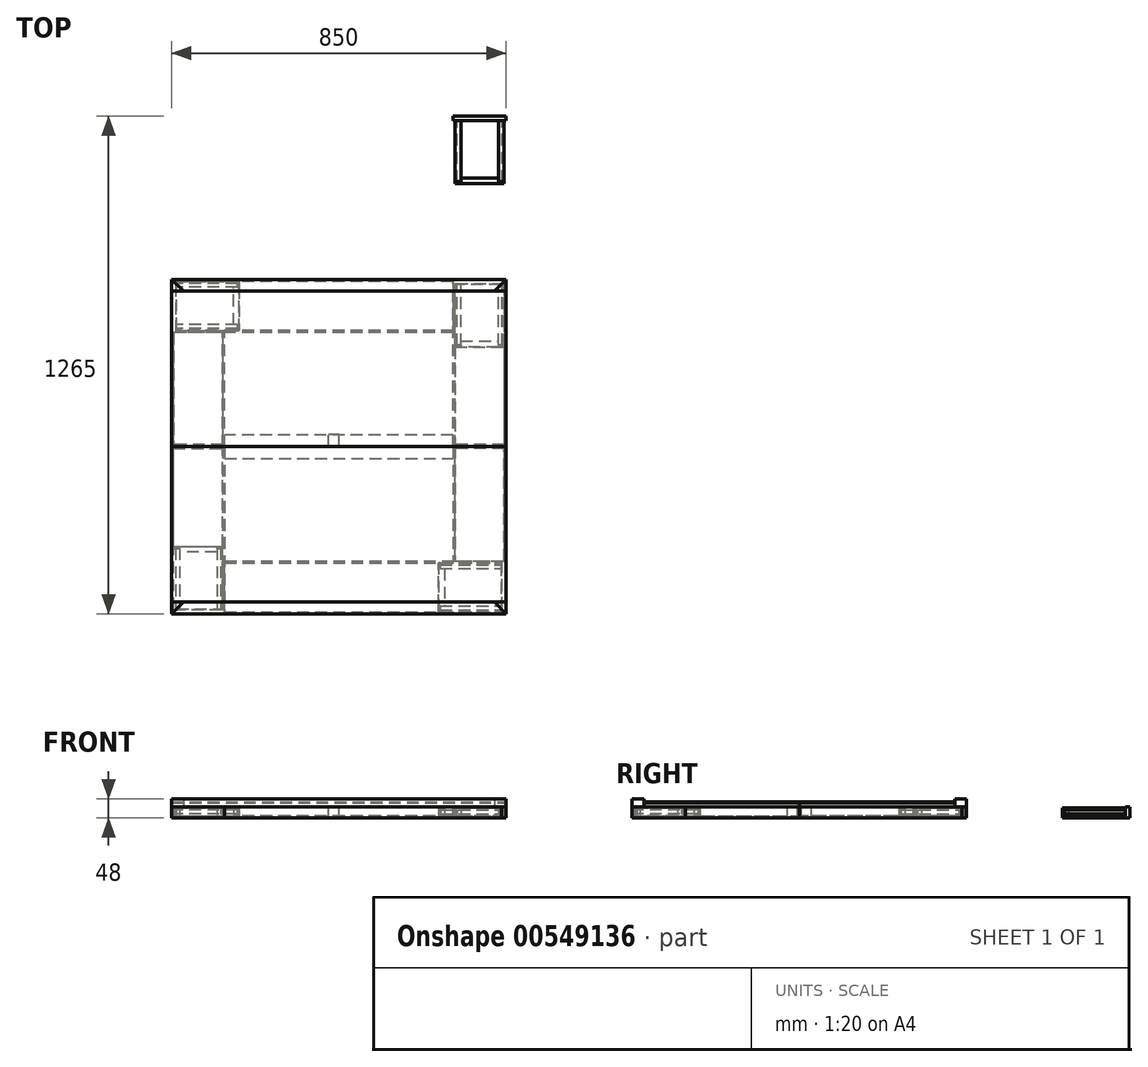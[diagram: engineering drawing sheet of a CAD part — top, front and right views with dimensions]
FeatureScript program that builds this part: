
annotation { "Feature Type Name" : "Feature", "Feature Type Description" : "" }
export const myFeature = defineFeature(function(context is Context, id is Id, definition is map)
    precondition{}
    {
        {
            var Q0;
            Q0=qCreatedBy(makeId("Front.planeOp"),FACE);
            var sketch = newSketch(context, id + "F0", { "sketchPlane" : qUnion([Q0])});
            skLineSegment(sketch, "E0.bottom", {"start": v(425, -17.5) * mm, "end": v(-425, -17.5) * mm});
            skLineSegment(sketch, "E0.top", {"start": v(425, 17.5) * mm, "end": v(-425, 17.5) * mm});
            skLineSegment(sketch, "E0.left", {"start": v(425, -17.5) * mm, "end": v(425, 17.5) * mm});
            skLineSegment(sketch, "E0.right", {"start": v(-425, -17.5) * mm, "end": v(-425, 17.5) * mm});
            skPoint(sketch, "E0.middle", {"position": v(0, 0) * mm});
            skLineSegment(sketch, "E1", {"start": v(-300, -17.5) * mm, "end": v(-300, 7.5) * mm});
            skLineSegment(sketch, "E2", {"start": v(-300, 7.5) * mm, "end": v(0, 7.5) * mm});
            skLineSegment(sketch, "E3", {"start": v(0, 7.5) * mm, "end": v(0, -34.56) * mm, "construction": true});
            skLineSegment(sketch, "E4.MirrorCS", {"start": v(300, 7.5) * mm, "end": v(0, 7.5) * mm});
            skLineSegment(sketch, "E5.MirrorCS", {"start": v(300, -17.5) * mm, "end": v(300, 7.5) * mm});
            skSolve(sketch);
        }
        {
            var Q0;
            Q0=qCreatedBy(makeId("Top.planeOp"),FACE);
            var sketch = newSketch(context, id + "F1", { "sketchPlane" : qUnion([Q0])});
            skLineSegment(sketch, "E6.bottom", {"start": v(425, -425) * mm, "end": v(-425, -425) * mm});
            skLineSegment(sketch, "E6.top", {"start": v(425, 425) * mm, "end": v(-425, 425) * mm});
            skLineSegment(sketch, "E6.left", {"start": v(425, -425) * mm, "end": v(425, 425) * mm});
            skLineSegment(sketch, "E6.right", {"start": v(-425, -425) * mm, "end": v(-425, 425) * mm});
            skPoint(sketch, "E6.middle", {"position": v(0, 0) * mm});
            skLineSegment(sketch, "E7", {"start": v(-425, 0) * mm, "end": v(425, 0) * mm});
            skPoint(sketch, "E7.startSnap0", {"position": v(-425, 0) * mm});
            skSolve(sketch);
        }
        {
            var Q0;
            {var subQ0=sQuery(id+"F1.wireOp",EDGE,"E6.bottom");Q0=makeQuery(id+"F1.imprint","IMPRINT",FACE,{"disambiguationData":[TD([[makeQuery(id+"F1.imprint","IMPRINT",EDGE,{"derivedFrom":subQ0}),-1.0]])]});}
            extrude(context, id + "F2", {"entities" : qUnion([Q0]), "oppositeDirection" : true, "depth" : 10 * mm, "offsetDistance" : 25 * mm});
        }
        {
            var Q0;
            Q0=makeQuery(id+"F2.opExtrude","CAP_FACE",FACE,{"disambiguationData":[OSD([sQuery(id+"F1.wireOp",EDGE,"E6.bottom"),sQuery(id+"F1.wireOp",EDGE,"E6.left"),sQuery(id+"F1.wireOp",EDGE,"E6.right"),sQuery(id+"F1.wireOp",EDGE,"E7")])],"isStart":false});
            var sketch = newSketch(context, id + "F3", { "sketchPlane" : qUnion([Q0])});
            skLineSegment(sketch, "E8.bottom", {"start": v(-425, 0) * mm, "end": v(-290, 0) * mm});
            skLineSegment(sketch, "E8.top", {"start": v(-425, 425) * mm, "end": v(-290, 425) * mm});
            skLineSegment(sketch, "E8.left", {"start": v(-425, 0) * mm, "end": v(-425, 425) * mm});
            skLineSegment(sketch, "E8.right", {"start": v(-290, 0) * mm, "end": v(-290, 425) * mm});
            skLineSegment(sketch, "E9.bottom", {"start": v(425, 0) * mm, "end": v(290, 0) * mm});
            skLineSegment(sketch, "E9.top", {"start": v(425, 425) * mm, "end": v(290, 425) * mm});
            skLineSegment(sketch, "E9.left", {"start": v(425, 0) * mm, "end": v(425, 425) * mm});
            skLineSegment(sketch, "E9.right", {"start": v(290, 0) * mm, "end": v(290, 290) * mm});
            skLineSegment(sketch, "E10.bottom", {"start": v(-290, 0) * mm, "end": v(290, 0) * mm});
            skLineSegment(sketch, "E10.top", {"start": v(-290, 30) * mm, "end": v(290, 30) * mm});
            skLineSegment(sketch, "E10.left", {"start": v(-290, 0) * mm, "end": v(-290, 30) * mm});
            skLineSegment(sketch, "E10.right", {"start": v(290, 0) * mm, "end": v(290, 30) * mm});
            skLineSegment(sketch, "E11.bottom", {"start": v(-290, 425) * mm, "end": v(290, 425) * mm});
            skLineSegment(sketch, "E11.top", {"start": v(-290, 360) * mm, "end": v(290, 360) * mm, "construction": true});
            skLineSegment(sketch, "E11.left", {"start": v(-290, 425) * mm, "end": v(-290, 360) * mm});
            skLineSegment(sketch, "E11.right", {"start": v(290, 425) * mm, "end": v(290, 360) * mm});
            skLineSegment(sketch, "E12.0", {"start": v(-420, 5) * mm, "end": v(-420, 425) * mm});
            skLineSegment(sketch, "E12.1", {"start": v(-420, 5) * mm, "end": v(-295, 5) * mm});
            skLineSegment(sketch, "E12.2", {"start": v(-295, 5) * mm, "end": v(-295, 425) * mm});
            skLineSegment(sketch, "E13", {"start": v(-420, 5) * mm, "end": v(-420, 0) * mm});
            skLineSegment(sketch, "E14", {"start": v(-295, 5) * mm, "end": v(-295, 0) * mm});
            skLineSegment(sketch, "E15", {"start": v(290, 290) * mm, "end": v(-290, 290) * mm});
            skLineSegment(sketch, "E16.0", {"start": v(425, 420) * mm, "end": v(290, 420) * mm});
            skLineSegment(sketch, "E16.1", {"start": v(-290, 420) * mm, "end": v(290, 420) * mm});
            skLineSegment(sketch, "E17", {"start": v(290, 290) * mm, "end": v(425, 290) * mm});
            skLineSegment(sketch, "E18.0", {"start": v(290, 295) * mm, "end": v(-290, 295) * mm});
            skLineSegment(sketch, "E18.1", {"start": v(290, 295) * mm, "end": v(425, 295) * mm});
            skLineSegment(sketch, "E19.trimOffspring", {"start": v(-285, 295) * mm, "end": v(-285, 420) * mm});
            skLineSegment(sketch, "E20.0", {"start": v(295, 0) * mm, "end": v(295, 290) * mm});
            skLineSegment(sketch, "E21.0", {"start": v(420, 0) * mm, "end": v(420, 290) * mm});
            skLineSegment(sketch, "E22.trimOffspring", {"start": v(290, 295) * mm, "end": v(290, 425) * mm});
            skLineSegment(sketch, "E23.0", {"start": v(420, 5) * mm, "end": v(295, 5) * mm});
            skSolve(sketch);
        }
        {
            var Q0;
            {var subQ0=sQuery(id+"F3.wireOp",EDGE,"E8.left");Q0=makeQuery(id+"F3.imprint","IMPRINT",FACE,{"disambiguationData":[TD([[makeQuery(id+"F3.imprint","IMPRINT",EDGE,{"derivedFrom":subQ0}),1.0]])]});}
            var Q1;
            Q1=makeQuery(id+"F3.imprint","IMPRINT",FACE,{"disambiguationData":[TD([[makeQuery(id+"F3.imprint","IMPRINT",EDGE,{"derivedFrom":sQuery(id+"F3.wireOp",EDGE,"E8.right")}),1.0]])]});
            var Q2;
            {var subQ1=sQuery(id+"F3.wireOp",EDGE,"E9.right");Q2=makeQuery(id+"F3.imprint","IMPRINT",FACE,{"disambiguationData":[TD([[makeQuery(id+"F3.imprint","IMPRINT",EDGE,{"derivedFrom":subQ1}),-1.0]])]});}
            var Q3;
            {var subQ3=sQuery(id+"F3.wireOp",EDGE,"E21.0");Q3=makeQuery(id+"F3.imprint","IMPRINT",FACE,{"disambiguationData":[TD([[makeQuery(id+"F3.imprint","IMPRINT",EDGE,{"derivedFrom":subQ3}),-1.0]])]});}
            extrude(context, id + "F4", {"entities" : qUnion([Q0, Q1, Q2, Q3]), "depth" : 28 * mm, "offsetDistance" : 25 * mm});
        }
        {
            var Q0;
            Q0=makeQuery(id+"F2.opExtrude","CAP_FACE",FACE,{"disambiguationData":[OSD([sQuery(id+"F1.wireOp",EDGE,"E6.bottom"),sQuery(id+"F1.wireOp",EDGE,"E6.left"),sQuery(id+"F1.wireOp",EDGE,"E6.right"),sQuery(id+"F1.wireOp",EDGE,"E7")])],"isStart":true});
            var sketch = newSketch(context, id + "F5", { "sketchPlane" : qUnion([Q0])});
            skLineSegment(sketch, "E24.bottom", {"start": v(-425, -425) * mm, "end": v(425, -425) * mm});
            skLineSegment(sketch, "E24.top", {"start": v(-425, -395) * mm, "end": v(425, -395) * mm});
            skLineSegment(sketch, "E24.left", {"start": v(-425, -425) * mm, "end": v(-425, -395) * mm});
            skLineSegment(sketch, "E24.right", {"start": v(425, -425) * mm, "end": v(425, -395) * mm});
            skLineSegment(sketch, "E25.bottom", {"start": v(-425, -395) * mm, "end": v(-395, -395) * mm});
            skLineSegment(sketch, "E25.top", {"start": v(-425, 0) * mm, "end": v(-395, 0) * mm});
            skLineSegment(sketch, "E25.left", {"start": v(-425, -395) * mm, "end": v(-425, 0) * mm});
            skLineSegment(sketch, "E25.right", {"start": v(-395, -395) * mm, "end": v(-395, 0) * mm});
            skLineSegment(sketch, "E26.bottom", {"start": v(425, -395) * mm, "end": v(395, -395) * mm});
            skLineSegment(sketch, "E26.top", {"start": v(425, 0) * mm, "end": v(395, 0) * mm});
            skLineSegment(sketch, "E26.left", {"start": v(425, -395) * mm, "end": v(425, 0) * mm});
            skLineSegment(sketch, "E26.right", {"start": v(395, -395) * mm, "end": v(395, 0) * mm});
            skLineSegment(sketch, "E27", {"start": v(-425, -425) * mm, "end": v(-395, -395) * mm});
            skLineSegment(sketch, "E28", {"start": v(395, -395) * mm, "end": v(425, -425) * mm});
            skSolve(sketch);
        }
        {
            var Q0;
            Q0=makeQuery(id+"F5.imprint","IMPRINT",FACE,{"disambiguationData":[TD([[makeQuery(id+"F5.imprint","IMPRINT",EDGE,{"derivedFrom":sQuery(id+"F5.wireOp",EDGE,"E24.bottom")}),-1.0]])]});
            extrude(context, id + "F6", {"entities" : qUnion([Q0]), "depth" : 10 * mm, "offsetDistance" : 25 * mm, "hasSecondDirection" : true, "secondDirectionOppositeDirection" : true, "secondDirectionDepth" : 10 * mm});
        }
        {
            var Q0;
            Q0=makeQuery(id+"F5.imprint","IMPRINT",FACE,{"disambiguationData":[TD([[makeQuery(id+"F5.imprint","IMPRINT",EDGE,{"derivedFrom":sQuery(id+"F5.wireOp",EDGE,"E25.bottom")}),1.0]])]});
            var Q1;
            Q1=makeQuery(id+"F5.imprint","IMPRINT",FACE,{"disambiguationData":[TD([[makeQuery(id+"F5.imprint","IMPRINT",EDGE,{"derivedFrom":sQuery(id+"F5.wireOp",EDGE,"E24.left")}),-1.0]])]});
            var Q2;
            Q2=makeQuery(id+"F5.imprint","IMPRINT",FACE,{"disambiguationData":[TD([[makeQuery(id+"F5.imprint","IMPRINT",EDGE,{"derivedFrom":sQuery(id+"F5.wireOp",EDGE,"E26.bottom")}),-1.0]])]});
            var Q3;
            Q3=makeQuery(id+"F5.imprint","IMPRINT",FACE,{"disambiguationData":[TD([[makeQuery(id+"F5.imprint","IMPRINT",EDGE,{"derivedFrom":sQuery(id+"F5.wireOp",EDGE,"E24.right")}),1.0]])]});
            var Q4;
            Q4=makeQuery(id+"F6.opExtrude","CAP_FACE",FACE,{"disambiguationData":[OSD([sQuery(id+"F5.wireOp",EDGE,"E24.bottom"),sQuery(id+"F5.wireOp",EDGE,"E24.top"),sQuery(id+"F5.wireOp",EDGE,"E27"),sQuery(id+"F5.wireOp",EDGE,"E28")])],"isStart":false});
            extrude(context, id + "F7", {"entities" : qUnion([Q0, Q1, Q2, Q3]), "endBound" : BoundingType.UP_TO_SURFACE, "depth" : 10 * mm, "endBoundEntityFace" : qUnion([Q4]), "offsetDistance" : 25 * mm, "hasSecondDirection" : true, "secondDirectionOppositeDirection" : true, "secondDirectionDepth" : 10 * mm});
        }
        {
            var Q0;
            Q0=makeQuery(id+"F7.opExtrude","SWEPT_BODY",BODY,{"disambiguationData":[OSD([sQuery(id+"F5.wireOp",EDGE,"E24.left"),sQuery(id+"F5.wireOp",EDGE,"E25.top"),sQuery(id+"F5.wireOp",EDGE,"E25.left"),sQuery(id+"F5.wireOp",EDGE,"E25.right"),sQuery(id+"F5.wireOp",EDGE,"E27")])]});
            var Q1;
            Q1=makeQuery(id+"F6.opExtrude","SWEPT_BODY",BODY,{"disambiguationData":[OSD([sQuery(id+"F5.wireOp",EDGE,"E24.bottom"),sQuery(id+"F5.wireOp",EDGE,"E24.top"),sQuery(id+"F5.wireOp",EDGE,"E27"),sQuery(id+"F5.wireOp",EDGE,"E28")])]});
            var Q2;
            Q2=makeQuery(id+"F7.opExtrude","SWEPT_BODY",BODY,{"disambiguationData":[OSD([sQuery(id+"F5.wireOp",EDGE,"E24.right"),sQuery(id+"F5.wireOp",EDGE,"E26.top"),sQuery(id+"F5.wireOp",EDGE,"E26.left"),sQuery(id+"F5.wireOp",EDGE,"E26.right"),sQuery(id+"F5.wireOp",EDGE,"E28")])]});
            var Q3;
            Q3=makeQuery(id+"F2.opExtrude","SWEPT_BODY",BODY,{"disambiguationData":[OSD([sQuery(id+"F1.wireOp",EDGE,"E6.bottom"),sQuery(id+"F1.wireOp",EDGE,"E6.left"),sQuery(id+"F1.wireOp",EDGE,"E6.right"),sQuery(id+"F1.wireOp",EDGE,"E7")])]});
            booleanBodies(context, id + "F8", {"operationType" : BooleanOperationType.SUBTRACTION, "tools" : qUnion([Q0, Q1, Q2]), "targets" : qUnion([Q3]), "keepTools" : true});
        }
        {
            var Q0;
            Q0=makeQuery(id+"F4.opExtrude","SWEPT_FACE",FACE,{"disambiguationData":[OSD([sQuery(id+"F3.wireOp",EDGE,"E8.top")])]});
            var sketch = newSketch(context, id + "F9", { "sketchPlane" : qUnion([Q0])});
            skLineSegment(sketch, "E29.bottom", {"start": v(-290, -10) * mm, "end": v(-425, -10) * mm});
            skLineSegment(sketch, "E29.top", {"start": v(-290, -38) * mm, "end": v(-425, -38) * mm});
            skLineSegment(sketch, "E29.left", {"start": v(-290, -10) * mm, "end": v(-290, -38) * mm});
            skLineSegment(sketch, "E29.right", {"start": v(-425, -10) * mm, "end": v(-425, -38) * mm});
            skSolve(sketch);
        }
        {
            var Q0;
            Q0=makeQuery(id+"F9.imprint","IMPRINT",FACE,{"disambiguationData":[TD([[makeQuery(id+"F9.imprint","IMPRINT",EDGE,{"derivedFrom":sQuery(id+"F9.wireOp",EDGE,"E29.bottom")}),1.0]])]});
            extrude(context, id + "F10", {"entities" : qUnion([Q0]), "oppositeDirection" : true, "depth" : 12 * mm, "offsetDistance" : 25 * mm});
        }
        {
            var Q0;
            Q0=makeQuery(id+"F10.opExtrude","SWEPT_BODY",BODY,{"disambiguationData":[OSD([sQuery(id+"F9.wireOp",EDGE,"E29.bottom"),sQuery(id+"F9.wireOp",EDGE,"E29.top"),sQuery(id+"F9.wireOp",EDGE,"E29.left"),sQuery(id+"F9.wireOp",EDGE,"E29.right")])]});
            var Q1;
            Q1=makeQuery(id+"F4.opExtrude","SWEPT_BODY",BODY,{"disambiguationData":[OSD([sQuery(id+"F3.wireOp",EDGE,"E8.bottom"),sQuery(id+"F3.wireOp",EDGE,"E8.top"),sQuery(id+"F3.wireOp",EDGE,"E8.left"),sQuery(id+"F3.wireOp",EDGE,"E8.right"),sQuery(id+"F3.wireOp",EDGE,"E10.left"),sQuery(id+"F3.wireOp",EDGE,"E11.left")])]});
            var Q2;
            Q2=makeQuery(id+"F4.opExtrude","SWEPT_BODY",BODY,{"disambiguationData":[OSD([sQuery(id+"F3.wireOp",EDGE,"E8.bottom"),sQuery(id+"F3.wireOp",EDGE,"E8.top"),sQuery(id+"F3.wireOp",EDGE,"E8.left"),sQuery(id+"F3.wireOp",EDGE,"E12.0"),sQuery(id+"F3.wireOp",EDGE,"E13")])]});
            booleanBodies(context, id + "F11", {"operationType" : BooleanOperationType.SUBTRACTION, "tools" : qUnion([Q0]), "targets" : qUnion([Q1, Q2]), "keepTools" : true});
        }
        {
            var Q0;
            Q0=makeQuery(id+"F4.opExtrude","CAP_FACE",FACE,{"disambiguationData":[OSD([sQuery(id+"F3.wireOp",EDGE,"E8.bottom"),sQuery(id+"F3.wireOp",EDGE,"E8.top"),sQuery(id+"F3.wireOp",EDGE,"E8.left"),sQuery(id+"F3.wireOp",EDGE,"E8.right"),sQuery(id+"F3.wireOp",EDGE,"E10.left"),sQuery(id+"F3.wireOp",EDGE,"E11.left")])],"isStart":false});
            var sketch = newSketch(context, id + "F12", { "sketchPlane" : qUnion([Q0])});
            skLineSegment(sketch, "E30.bottom", {"start": v(-420, 413) * mm, "end": v(-295, 413) * mm});
            skLineSegment(sketch, "E30.top", {"start": v(-420, 253) * mm, "end": v(-295, 253) * mm});
            skLineSegment(sketch, "E30.left", {"start": v(-420, 413) * mm, "end": v(-420, 253) * mm});
            skLineSegment(sketch, "E30.right", {"start": v(-295, 413) * mm, "end": v(-295, 253) * mm});
            skLineSegment(sketch, "E31.0", {"start": v(-310, 413) * mm, "end": v(-310, 268) * mm});
            skLineSegment(sketch, "E31.1", {"start": v(-405, 268) * mm, "end": v(-310, 268) * mm});
            skLineSegment(sketch, "E31.2", {"start": v(-405, 413) * mm, "end": v(-405, 268) * mm});
            skLineSegment(sketch, "E32", {"start": v(-405, 268) * mm, "end": v(-405, 253) * mm});
            skLineSegment(sketch, "E33", {"start": v(-310, 268) * mm, "end": v(-310, 253) * mm});
            skLineSegment(sketch, "E34.0", {"start": v(-420, 258) * mm, "end": v(-295, 258) * mm});
            skLineSegment(sketch, "E35.bottom", {"start": v(-295, 253) * mm, "end": v(-420, 253) * mm});
            skLineSegment(sketch, "E35.top", {"start": v(-295, 0) * mm, "end": v(-420, 0) * mm});
            skLineSegment(sketch, "E35.left", {"start": v(-295, 253) * mm, "end": v(-295, 0) * mm});
            skLineSegment(sketch, "E35.right", {"start": v(-420, 253) * mm, "end": v(-420, 0) * mm});
            skSolve(sketch);
        }
        {
            var Q0;
            {var subQ1=sQuery(id+"F12.wireOp",EDGE,"E31.0");Q0=makeQuery(id+"F12.imprint","IMPRINT",FACE,{"disambiguationData":[TD([[makeQuery(id+"F12.imprint","IMPRINT",EDGE,{"derivedFrom":subQ1}),1.0]])]});}
            var Q1;
            {var subQ1=sQuery(id+"F12.wireOp",EDGE,"E31.2");Q1=makeQuery(id+"F12.imprint","IMPRINT",FACE,{"disambiguationData":[TD([[makeQuery(id+"F12.imprint","IMPRINT",EDGE,{"derivedFrom":subQ1}),-1.0]])]});}
            extrude(context, id + "F13", {"entities" : qUnion([Q0, Q1]), "oppositeDirection" : true, "depth" : 25 * mm, "offsetDistance" : 25 * mm});
        }
        {
            var Q0;
            {var subQ0=sQuery(id+"F12.wireOp",EDGE,"E35.bottom");var subQ5=sQuery(id+"F12.wireOp",EDGE,"E33");var subQ6=makeQuery(id+"F12.imprint","INTERSECT",VERTEX,{"derivedFrom":[subQ5,subQ0]});Q0=makeQuery(id+"F12.imprint","IMPRINT",FACE,{"disambiguationData":[TD([[makeQuery(id+"F12.imprint","IMPRINT",EDGE,{"disambiguationData":[TD([[subQ6,1.0]])],"derivedFrom":subQ5}),1.0]])]});}
            var Q1;
            {var subQ0=sQuery(id+"F12.wireOp",EDGE,"E35.bottom");var subQ1=sQuery(id+"F12.wireOp",EDGE,"E32");var subQ2=makeQuery(id+"F12.imprint","INTERSECT",VERTEX,{"derivedFrom":[subQ1,subQ0]});Q1=makeQuery(id+"F12.imprint","IMPRINT",FACE,{"disambiguationData":[TD([[makeQuery(id+"F12.imprint","IMPRINT",EDGE,{"disambiguationData":[TD([[subQ2,1.0]])],"derivedFrom":subQ1}),1.0]])]});}
            var Q2;
            {var subQ0=sQuery(id+"F12.wireOp",EDGE,"E35.bottom");var subQ5=sQuery(id+"F12.wireOp",EDGE,"E32");var subQ7=makeQuery(id+"F12.imprint","INTERSECT",VERTEX,{"derivedFrom":[subQ5,subQ0]});Q2=makeQuery(id+"F12.imprint","IMPRINT",FACE,{"disambiguationData":[TD([[makeQuery(id+"F12.imprint","IMPRINT",EDGE,{"disambiguationData":[TD([[subQ7,1.0]])],"derivedFrom":subQ5}),-1.0]])]});}
            var Q3;
            Q3=makeQuery(id+"F13.opExtrude","CAP_FACE",FACE,{"disambiguationData":[OSD([sQuery(id+"F12.wireOp",EDGE,"E30.bottom"),sQuery(id+"F12.wireOp",EDGE,"E30.right"),sQuery(id+"F12.wireOp",EDGE,"E31.0"),sQuery(id+"F12.wireOp",EDGE,"E33"),sQuery(id+"F12.wireOp",EDGE,"E34.0")])],"isStart":false});
            extrude(context, id + "F14", {"entities" : qUnion([Q0, Q1, Q2]), "endBound" : BoundingType.UP_TO_SURFACE, "oppositeDirection" : true, "depth" : 5 * mm, "endBoundEntityFace" : qUnion([Q3]), "offsetDistance" : 25 * mm});
        }
        {
            var Q0;
            {var subQ0=sQuery(id+"F12.wireOp",EDGE,"E31.0");Q0=makeQuery(id+"F12.imprint","IMPRINT",FACE,{"disambiguationData":[TD([[makeQuery(id+"F12.imprint","IMPRINT",EDGE,{"derivedFrom":subQ0}),-1.0]])]});}
            var Q1;
            Q1=makeQuery(id+"F12.imprint","IMPRINT",FACE,{"disambiguationData":[TD([[makeQuery(id+"F12.imprint","IMPRINT",EDGE,{"derivedFrom":sQuery(id+"F12.wireOp",EDGE,"E31.1")}),-1.0]])]});
            var Q2;
            {var subQ0=sQuery(id+"F12.wireOp",EDGE,"E32");var subQ1=sQuery(id+"F12.wireOp",EDGE,"E30.top");var subQ2=makeQuery(id+"F12.imprint","INTERSECT",VERTEX,{"derivedFrom":[subQ1,subQ0]});Q2=makeQuery(id+"F12.imprint","IMPRINT",FACE,{"disambiguationData":[TD([[makeQuery(id+"F12.imprint","IMPRINT",EDGE,{"disambiguationData":[TD([[subQ2,-1.0]])],"derivedFrom":subQ1}),1.0]])]});}
            var Q3;
            {var subQ1=sQuery(id+"F12.wireOp",EDGE,"E31.0");Q3=makeQuery(id+"F12.imprint","IMPRINT",FACE,{"disambiguationData":[TD([[makeQuery(id+"F12.imprint","IMPRINT",EDGE,{"derivedFrom":subQ1}),1.0]])]});}
            var Q4;
            {var subQ1=sQuery(id+"F12.wireOp",EDGE,"E31.2");Q4=makeQuery(id+"F12.imprint","IMPRINT",FACE,{"disambiguationData":[TD([[makeQuery(id+"F12.imprint","IMPRINT",EDGE,{"derivedFrom":subQ1}),-1.0]])]});}
            extrude(context, id + "F15", {"entities" : qUnion([Q0, Q1, Q2, Q3, Q4]), "oppositeDirection" : true, "depth" : 5 * mm, "offsetDistance" : 25 * mm});
        }
        {
            var Q0;
            Q0=makeQuery(id+"F15.opExtrude","SWEPT_BODY",BODY,{"disambiguationData":[OSD([sQuery(id+"F12.wireOp",EDGE,"E30.bottom"),sQuery(id+"F12.wireOp",EDGE,"E30.top"),sQuery(id+"F12.wireOp",EDGE,"E30.left"),sQuery(id+"F12.wireOp",EDGE,"E30.right")])]});
            var Q1;
            Q1=makeQuery(id+"F13.opExtrude","SWEPT_BODY",BODY,{"disambiguationData":[OSD([sQuery(id+"F12.wireOp",EDGE,"E30.bottom"),sQuery(id+"F12.wireOp",EDGE,"E30.top"),sQuery(id+"F12.wireOp",EDGE,"E30.left"),sQuery(id+"F12.wireOp",EDGE,"E31.2"),sQuery(id+"F12.wireOp",EDGE,"E32")])]});
            var Q2;
            Q2=makeQuery(id+"F13.opExtrude","SWEPT_BODY",BODY,{"disambiguationData":[OSD([sQuery(id+"F12.wireOp",EDGE,"E30.bottom"),sQuery(id+"F12.wireOp",EDGE,"E30.top"),sQuery(id+"F12.wireOp",EDGE,"E30.right"),sQuery(id+"F12.wireOp",EDGE,"E31.0"),sQuery(id+"F12.wireOp",EDGE,"E33")])]});
            var Q3;
            Q3=makeQuery(id+"F14.opExtrude","SWEPT_BODY",BODY,{"disambiguationData":[OSD([sQuery(id+"F12.wireOp",EDGE,"E30.left"),sQuery(id+"F12.wireOp",EDGE,"E30.right"),sQuery(id+"F12.wireOp",EDGE,"E34.0"),sQuery(id+"F12.wireOp",EDGE,"E35.bottom")])]});
            booleanBodies(context, id + "F16", {"operationType" : BooleanOperationType.SUBTRACTION, "tools" : qUnion([Q0]), "targets" : qUnion([Q1, Q2, Q3]), "keepTools" : true});
        }
        {
            var Q0;
            {var subQ0=sQuery(id+"F12.wireOp",EDGE,"E30.bottom");Q0=makeQuery(id+"F13.opExtrude","SWEPT_FACE",FACE,{"disambiguationData":[OSD([subQ0]),TDD([makeQuery(id+"F12.imprint","IMPRINT",EDGE,{"disambiguationData":[TD([[makeQuery(id+"F12.imprint","INTERSECT",VERTEX,{"derivedFrom":[subQ0,sQuery(id+"F12.wireOp",EDGE,"E30.left")]}),-1.0]])],"derivedFrom":subQ0})])]});}
            var sketch = newSketch(context, id + "F17", { "sketchPlane" : qUnion([Q0])});
            skLineSegment(sketch, "E36.bottom", {"start": v(-420, -18) * mm, "end": v(-415, -18) * mm});
            skLineSegment(sketch, "E36.top", {"start": v(-420, -28) * mm, "end": v(-415, -28) * mm});
            skLineSegment(sketch, "E36.left", {"start": v(-420, -18) * mm, "end": v(-420, -28) * mm});
            skLineSegment(sketch, "E36.right", {"start": v(-415, -18) * mm, "end": v(-415, -28) * mm});
            skLineSegment(sketch, "E37", {"start": v(-408.16, -23) * mm, "end": v(-412.7, -23) * mm, "construction": true});
            skPoint(sketch, "E38", {"position": v(-415, -23) * mm});
            skLineSegment(sketch, "E39.bottom", {"start": v(-295, -18) * mm, "end": v(-300, -18) * mm});
            skLineSegment(sketch, "E39.top", {"start": v(-295, -28) * mm, "end": v(-300, -28) * mm});
            skLineSegment(sketch, "E39.left", {"start": v(-295, -18) * mm, "end": v(-295, -28) * mm});
            skLineSegment(sketch, "E39.right", {"start": v(-300, -18) * mm, "end": v(-300, -28) * mm});
            skSolve(sketch);
        }
        {
            var Q0;
            Q0=makeQuery(id+"F17.imprint","IMPRINT",FACE,{"disambiguationData":[TD([[makeQuery(id+"F17.imprint","IMPRINT",EDGE,{"derivedFrom":sQuery(id+"F17.wireOp",EDGE,"E36.bottom")}),-1.0]])]});
            var Q1;
            Q1=makeQuery(id+"F17.imprint","IMPRINT",FACE,{"disambiguationData":[TD([[makeQuery(id+"F17.imprint","IMPRINT",EDGE,{"derivedFrom":sQuery(id+"F17.wireOp",EDGE,"E39.bottom")}),1.0]])]});
            extrude(context, id + "F18", {"entities" : qUnion([Q0, Q1]), "oppositeDirection" : true, "depth" : 60 * mm, "offsetDistance" : 25 * mm});
        }
        {
            var Q0;
            Q0=makeQuery(id+"F18.opExtrude","SWEPT_BODY",BODY,{"disambiguationData":[OSD([sQuery(id+"F17.wireOp",EDGE,"E39.bottom"),sQuery(id+"F17.wireOp",EDGE,"E39.top"),sQuery(id+"F17.wireOp",EDGE,"E39.left"),sQuery(id+"F17.wireOp",EDGE,"E39.right")])]});
            var Q1;
            Q1=makeQuery(id+"F18.opExtrude","SWEPT_BODY",BODY,{"disambiguationData":[OSD([sQuery(id+"F17.wireOp",EDGE,"E36.bottom"),sQuery(id+"F17.wireOp",EDGE,"E36.top"),sQuery(id+"F17.wireOp",EDGE,"E36.left"),sQuery(id+"F17.wireOp",EDGE,"E36.right")])]});
            var Q2;
            Q2=makeQuery(id+"F13.opExtrude","SWEPT_BODY",BODY,{"disambiguationData":[OSD([sQuery(id+"F12.wireOp",EDGE,"E30.bottom"),sQuery(id+"F12.wireOp",EDGE,"E30.top"),sQuery(id+"F12.wireOp",EDGE,"E30.left"),sQuery(id+"F12.wireOp",EDGE,"E31.2"),sQuery(id+"F12.wireOp",EDGE,"E32")])]});
            var Q3;
            Q3=makeQuery(id+"F13.opExtrude","SWEPT_BODY",BODY,{"disambiguationData":[OSD([sQuery(id+"F12.wireOp",EDGE,"E30.bottom"),sQuery(id+"F12.wireOp",EDGE,"E30.top"),sQuery(id+"F12.wireOp",EDGE,"E30.right"),sQuery(id+"F12.wireOp",EDGE,"E31.0"),sQuery(id+"F12.wireOp",EDGE,"E33")])]});
            booleanBodies(context, id + "F19", {"operationType" : BooleanOperationType.SUBTRACTION, "tools" : qUnion([Q0, Q1]), "targets" : qUnion([Q2, Q3]), "keepTools" : true});
        }
        {
            var Q0;
            Q0=makeQuery(id+"F3.imprint","IMPRINT",FACE,{"disambiguationData":[TD([[makeQuery(id+"F3.imprint","IMPRINT",EDGE,{"derivedFrom":sQuery(id+"F3.wireOp",EDGE,"E12.1")}),-1.0]])]});
            var Q1;
            {var subQ5=sQuery(id+"F3.wireOp",EDGE,"E23.0");Q1=makeQuery(id+"F3.imprint","IMPRINT",FACE,{"disambiguationData":[TD([[makeQuery(id+"F3.imprint","IMPRINT",EDGE,{"derivedFrom":subQ5}),1.0]])]});}
            var Q2;
            Q2=makeQuery(id+"F4.opExtrude","CAP_FACE",FACE,{"disambiguationData":[OSD([sQuery(id+"F3.wireOp",EDGE,"E8.bottom"),sQuery(id+"F3.wireOp",EDGE,"E8.top"),sQuery(id+"F3.wireOp",EDGE,"E8.left"),sQuery(id+"F3.wireOp",EDGE,"E12.0"),sQuery(id+"F3.wireOp",EDGE,"E13")])],"isStart":false});
            extrude(context, id + "F20", {"entities" : qUnion([Q0, Q1]), "endBound" : BoundingType.UP_TO_SURFACE, "depth" : 25 * mm, "endBoundEntityFace" : qUnion([Q2]), "offsetDistance" : 25 * mm});
        }
        {
            var Q0;
            Q0=makeQuery(id+"F12.imprint","IMPRINT",FACE,{"disambiguationData":[TD([[makeQuery(id+"F12.imprint","IMPRINT",EDGE,{"derivedFrom":sQuery(id+"F12.wireOp",EDGE,"E35.top")}),-1.0]])]});
            extrude(context, id + "F21", {"entities" : qUnion([Q0]), "oppositeDirection" : true, "depth" : 5 * mm, "offsetDistance" : 25 * mm});
        }
        {
            var Q0;
            Q0=makeQuery(id+"F20.opExtrude","SWEPT_BODY",BODY,{"disambiguationData":[OSD([sQuery(id+"F3.wireOp",EDGE,"E8.bottom"),sQuery(id+"F3.wireOp",EDGE,"E12.1"),sQuery(id+"F3.wireOp",EDGE,"E13"),sQuery(id+"F3.wireOp",EDGE,"E14")])]});
            var Q1;
            Q1=makeQuery(id+"F21.opExtrude","SWEPT_BODY",BODY,{"disambiguationData":[OSD([sQuery(id+"F12.wireOp",EDGE,"E35.bottom"),sQuery(id+"F12.wireOp",EDGE,"E35.top"),sQuery(id+"F12.wireOp",EDGE,"E35.left"),sQuery(id+"F12.wireOp",EDGE,"E35.right")])]});
            booleanBodies(context, id + "F22", {"operationType" : BooleanOperationType.SUBTRACTION, "tools" : qUnion([Q0]), "targets" : qUnion([Q1]), "keepTools" : true});
        }
        {
            var Q0;
            Q0=makeQuery(id+"F2.opExtrude","CAP_FACE",FACE,{"disambiguationData":[OSD([sQuery(id+"F1.wireOp",EDGE,"E6.bottom"),sQuery(id+"F1.wireOp",EDGE,"E6.left"),sQuery(id+"F1.wireOp",EDGE,"E6.right"),sQuery(id+"F1.wireOp",EDGE,"E7")])],"isStart":false});
            var sketch = newSketch(context, id + "F23", { "sketchPlane" : qUnion([Q0])});
            skLineSegment(sketch, "E40.bottom", {"start": v(425, 425) * mm, "end": v(-425, 425) * mm, "construction": true});
            skLineSegment(sketch, "E40.top", {"start": v(425, 0) * mm, "end": v(-425, 0) * mm, "construction": true});
            skLineSegment(sketch, "E40.left", {"start": v(425, 425) * mm, "end": v(425, 0) * mm, "construction": true});
            skLineSegment(sketch, "E40.right", {"start": v(-425, 425) * mm, "end": v(-425, 0) * mm, "construction": true});
            skLineSegment(sketch, "E41.bottom", {"start": v(0, 0) * mm, "end": v(-26.25, 0) * mm});
            skLineSegment(sketch, "E41.top", {"start": v(0, -31.08) * mm, "end": v(-26.25, -31.08) * mm});
            skLineSegment(sketch, "E41.left", {"start": v(0, 0) * mm, "end": v(0, -31.08) * mm});
            skLineSegment(sketch, "E41.right", {"start": v(-26.25, 0) * mm, "end": v(-26.25, -31.08) * mm});
            skSolve(sketch);
        }
        {
            var Q0;
            Q0=makeQuery(id+"F23.imprint","IMPRINT",FACE,{"disambiguationData":[TD([[makeQuery(id+"F23.imprint","IMPRINT",EDGE,{"derivedFrom":sQuery(id+"F23.wireOp",EDGE,"E41.bottom")}),-1.0]])]});
            extrude(context, id + "F24", {"entities" : qUnion([Q0]), "depth" : 25 * mm, "offsetDistance" : 25 * mm});
        }
        {
            var Q0;
            Q0=makeQuery(id+"F17.imprint","IMPRINT",FACE,{"disambiguationData":[TD([[makeQuery(id+"F17.imprint","IMPRINT",EDGE,{"derivedFrom":sQuery(id+"F17.wireOp",EDGE,"E36.bottom")}),-1.0]])]});
            var Q1;
            Q1=makeQuery(id+"F17.imprint","IMPRINT",FACE,{"disambiguationData":[TD([[makeQuery(id+"F17.imprint","IMPRINT",EDGE,{"derivedFrom":sQuery(id+"F17.wireOp",EDGE,"E39.bottom")}),1.0]])]});
            var Q2;
            Q2=makeQuery(id+"F14.opExtrude","SWEPT_FACE",FACE,{"disambiguationData":[OSD([sQuery(id+"F12.wireOp",EDGE,"E34.0")])]});
            extrude(context, id + "F25", {"entities" : qUnion([Q0, Q1]), "operationType" : NewBodyOperationType.REMOVE, "endBound" : BoundingType.UP_TO_SURFACE, "oppositeDirection" : true, "depth" : 25 * mm, "endBoundEntityFace" : qUnion([Q2]), "offsetDistance" : 25 * mm});
        }
        {
            var Q0;
            Q0=makeQuery(id+"F10.opExtrude","SWEPT_BODY",BODY,{"disambiguationData":[OSD([sQuery(id+"F9.wireOp",EDGE,"E29.bottom"),sQuery(id+"F9.wireOp",EDGE,"E29.top"),sQuery(id+"F9.wireOp",EDGE,"E29.left"),sQuery(id+"F9.wireOp",EDGE,"E29.right")])]});
            var Q1;
            Q1=makeQuery(id+"F13.opExtrude","SWEPT_BODY",BODY,{"disambiguationData":[OSD([sQuery(id+"F12.wireOp",EDGE,"E30.bottom"),sQuery(id+"F12.wireOp",EDGE,"E30.right"),sQuery(id+"F12.wireOp",EDGE,"E31.0"),sQuery(id+"F12.wireOp",EDGE,"E33"),sQuery(id+"F12.wireOp",EDGE,"E34.0")])]});
            var Q2;
            Q2=makeQuery(id+"F13.opExtrude","SWEPT_BODY",BODY,{"disambiguationData":[OSD([sQuery(id+"F12.wireOp",EDGE,"E30.bottom"),sQuery(id+"F12.wireOp",EDGE,"E30.left"),sQuery(id+"F12.wireOp",EDGE,"E31.2"),sQuery(id+"F12.wireOp",EDGE,"E32"),sQuery(id+"F12.wireOp",EDGE,"E34.0")])]});
            var Q3;
            Q3=makeQuery(id+"F14.opExtrude","SWEPT_BODY",BODY,{"disambiguationData":[OSD([sQuery(id+"F12.wireOp",EDGE,"E30.left"),sQuery(id+"F12.wireOp",EDGE,"E30.right"),sQuery(id+"F12.wireOp",EDGE,"E34.0"),sQuery(id+"F12.wireOp",EDGE,"E35.bottom")])]});
            var Q4;
            Q4=makeQuery(id+"F15.opExtrude","SWEPT_BODY",BODY,{"disambiguationData":[OSD([sQuery(id+"F12.wireOp",EDGE,"E30.bottom"),sQuery(id+"F12.wireOp",EDGE,"E30.left"),sQuery(id+"F12.wireOp",EDGE,"E30.right"),sQuery(id+"F12.wireOp",EDGE,"E35.bottom")])]});
            var Q5;
            Q5=makeQuery(id+"F18.opExtrude","SWEPT_BODY",BODY,{"disambiguationData":[OSD([sQuery(id+"F17.wireOp",EDGE,"E36.bottom"),sQuery(id+"F17.wireOp",EDGE,"E36.top"),sQuery(id+"F17.wireOp",EDGE,"E36.left"),sQuery(id+"F17.wireOp",EDGE,"E36.right")])]});
            var Q6;
            Q6=makeQuery(id+"F18.opExtrude","SWEPT_BODY",BODY,{"disambiguationData":[OSD([sQuery(id+"F17.wireOp",EDGE,"E39.bottom"),sQuery(id+"F17.wireOp",EDGE,"E39.top"),sQuery(id+"F17.wireOp",EDGE,"E39.left"),sQuery(id+"F17.wireOp",EDGE,"E39.right")])]});
            var Q7;
            Q7=makeQuery(id+"F24.opExtrude","SWEPT_EDGE",EDGE,{"disambiguationData":[OSD([sQuery(id+"F1.wireOp",EDGE,"E7"),sQuery(id+"F23.wireOp",EDGE,"E41.bottom"),sQuery(id+"F23.wireOp",EDGE,"E41.left")])]});
            circularPattern(context, id + "F26", {"entities" : qUnion([Q0, Q1, Q2, Q3, Q4, Q5, Q6]), "axis" : qUnion([Q7]), "angle" : 90 * degree, "instanceCount" : 2, "equalSpace" : true});
        }
        {
            var Q0;
            {var subQ4=sQuery(id+"F3.wireOp",EDGE,"E11.bottom");Q0=makeQuery(id+"F3.imprint","IMPRINT",FACE,{"disambiguationData":[TD([[makeQuery(id+"F3.imprint","IMPRINT",EDGE,{"derivedFrom":subQ4}),1.0]])]});}
            var Q1;
            {var subQ0=sQuery(id+"F3.wireOp",EDGE,"E15");Q1=makeQuery(id+"F3.imprint","IMPRINT",FACE,{"disambiguationData":[TD([[makeQuery(id+"F3.imprint","IMPRINT",EDGE,{"derivedFrom":subQ0}),-1.0]])]});}
            var Q2;
            {var subQ0=sQuery(id+"F3.wireOp",EDGE,"E9.top");Q2=makeQuery(id+"F3.imprint","IMPRINT",FACE,{"disambiguationData":[TD([[makeQuery(id+"F3.imprint","IMPRINT",EDGE,{"derivedFrom":subQ0}),1.0]])]});}
            var Q3;
            {var subQ0=sQuery(id+"F3.wireOp",EDGE,"E17");Q3=makeQuery(id+"F3.imprint","IMPRINT",FACE,{"disambiguationData":[TD([[makeQuery(id+"F3.imprint","IMPRINT",EDGE,{"derivedFrom":subQ0}),1.0]])]});}
            var Q4;
            Q4=makeQuery(id+"F4.opExtrude","CAP_FACE",FACE,{"disambiguationData":[OSD([sQuery(id+"F3.wireOp",EDGE,"E8.bottom"),sQuery(id+"F3.wireOp",EDGE,"E8.top"),sQuery(id+"F3.wireOp",EDGE,"E8.right"),sQuery(id+"F3.wireOp",EDGE,"E10.left"),sQuery(id+"F3.wireOp",EDGE,"E11.left"),sQuery(id+"F3.wireOp",EDGE,"E12.2"),sQuery(id+"F3.wireOp",EDGE,"E14")])],"isStart":false});
            extrude(context, id + "F27", {"entities" : qUnion([Q0, Q1, Q2, Q3]), "endBound" : BoundingType.UP_TO_SURFACE, "depth" : 25 * mm, "endBoundEntityFace" : qUnion([Q4]), "offsetDistance" : 25 * mm});
        }
        {
            var Q0;
            Q0=makeQuery(id+"F26.opPattern","COPY",BODY,{"derivedFrom":makeQuery(id+"F10.opExtrude","SWEPT_BODY",BODY,{"disambiguationData":[OSD([sQuery(id+"F9.wireOp",EDGE,"E29.bottom"),sQuery(id+"F9.wireOp",EDGE,"E29.top"),sQuery(id+"F9.wireOp",EDGE,"E29.left"),sQuery(id+"F9.wireOp",EDGE,"E29.right")])]}),"instanceName":"1"});
            var Q1;
            Q1=makeQuery(id+"F27.opExtrude","SWEPT_BODY",BODY,{"disambiguationData":[OSD([sQuery(id+"F3.wireOp",EDGE,"E9.top"),sQuery(id+"F3.wireOp",EDGE,"E9.left"),sQuery(id+"F3.wireOp",EDGE,"E11.bottom"),sQuery(id+"F3.wireOp",EDGE,"E11.left"),sQuery(id+"F3.wireOp",EDGE,"E16.0"),sQuery(id+"F3.wireOp",EDGE,"E16.1")])]});
            var Q2;
            Q2=makeQuery(id+"F27.opExtrude","SWEPT_BODY",BODY,{"disambiguationData":[OSD([sQuery(id+"F3.wireOp",EDGE,"E8.right"),sQuery(id+"F3.wireOp",EDGE,"E9.left"),sQuery(id+"F3.wireOp",EDGE,"E15"),sQuery(id+"F3.wireOp",EDGE,"E17"),sQuery(id+"F3.wireOp",EDGE,"E18.0"),sQuery(id+"F3.wireOp",EDGE,"E18.1")])]});
            booleanBodies(context, id + "F28", {"operationType" : BooleanOperationType.SUBTRACTION, "tools" : qUnion([Q0]), "targets" : qUnion([Q1, Q2]), "keepTools" : true});
        }
        {
            var Q0;
            Q0=makeQuery(id+"F21.opExtrude","CAP_FACE",FACE,{"disambiguationData":[OSD([sQuery(id+"F12.wireOp",EDGE,"E35.bottom"),sQuery(id+"F12.wireOp",EDGE,"E35.top"),sQuery(id+"F12.wireOp",EDGE,"E35.left"),sQuery(id+"F12.wireOp",EDGE,"E35.right")])],"isStart":true});
            var sketch = newSketch(context, id + "F29", { "sketchPlane" : qUnion([Q0])});
            skLineSegment(sketch, "E42.bottom", {"start": v(-290, 420) * mm, "end": v(253, 420) * mm});
            skLineSegment(sketch, "E42.top", {"start": v(-290, 295) * mm, "end": v(253, 295) * mm});
            skLineSegment(sketch, "E42.left", {"start": v(-290, 420) * mm, "end": v(-290, 295) * mm});
            skLineSegment(sketch, "E42.right", {"start": v(253, 420) * mm, "end": v(253, 295) * mm});
            skLineSegment(sketch, "E43.bottom", {"start": v(295, 290) * mm, "end": v(420, 290) * mm});
            skLineSegment(sketch, "E43.top", {"start": v(295, 5) * mm, "end": v(420, 5) * mm});
            skLineSegment(sketch, "E43.left", {"start": v(295, 290) * mm, "end": v(295, 5) * mm});
            skLineSegment(sketch, "E43.right", {"start": v(420, 290) * mm, "end": v(420, 5) * mm});
            skSolve(sketch);
        }
        {
            var Q0;
            Q0=makeQuery(id+"F29.imprint","IMPRINT",FACE,{"disambiguationData":[TD([[makeQuery(id+"F29.imprint","IMPRINT",EDGE,{"derivedFrom":sQuery(id+"F29.wireOp",EDGE,"E42.bottom")}),-1.0]])]});
            var Q1;
            Q1=makeQuery(id+"F29.imprint","IMPRINT",FACE,{"disambiguationData":[TD([[makeQuery(id+"F29.imprint","IMPRINT",EDGE,{"derivedFrom":sQuery(id+"F29.wireOp",EDGE,"E43.bottom")}),-1.0]])]});
            extrude(context, id + "F30", {"entities" : qUnion([Q0, Q1]), "oppositeDirection" : true, "depth" : 5 * mm, "offsetDistance" : 25 * mm});
        }
        {
            var Q0;
            Q0=makeQuery(id+"F3.imprint","IMPRINT",FACE,{"disambiguationData":[TD([[makeQuery(id+"F3.imprint","IMPRINT",EDGE,{"derivedFrom":sQuery(id+"F3.wireOp",EDGE,"E10.bottom")}),1.0]])]});
            var Q1;
            Q1=makeQuery(id+"F21.opExtrude","CAP_FACE",FACE,{"disambiguationData":[OSD([sQuery(id+"F12.wireOp",EDGE,"E35.bottom"),sQuery(id+"F12.wireOp",EDGE,"E35.top"),sQuery(id+"F12.wireOp",EDGE,"E35.left"),sQuery(id+"F12.wireOp",EDGE,"E35.right")])],"isStart":true});
            extrude(context, id + "F31", {"entities" : qUnion([Q0]), "endBound" : BoundingType.UP_TO_SURFACE, "depth" : 25 * mm, "endBoundEntityFace" : qUnion([Q1]), "offsetDistance" : 25 * mm});
        }
        {
            var Q0;
            Q0=makeQuery(id+"F2.opExtrude","SWEPT_BODY",BODY,{"disambiguationData":[OSD([sQuery(id+"F1.wireOp",EDGE,"E6.bottom"),sQuery(id+"F1.wireOp",EDGE,"E6.left"),sQuery(id+"F1.wireOp",EDGE,"E6.right"),sQuery(id+"F1.wireOp",EDGE,"E7")])]});
            var Q1;
            Q1=makeQuery(id+"F10.opExtrude","SWEPT_BODY",BODY,{"disambiguationData":[OSD([sQuery(id+"F9.wireOp",EDGE,"E29.bottom"),sQuery(id+"F9.wireOp",EDGE,"E29.top"),sQuery(id+"F9.wireOp",EDGE,"E29.left"),sQuery(id+"F9.wireOp",EDGE,"E29.right")])]});
            var Q2;
            Q2=makeQuery(id+"F27.opExtrude","SWEPT_BODY",BODY,{"disambiguationData":[OSD([sQuery(id+"F3.wireOp",EDGE,"E9.top"),sQuery(id+"F3.wireOp",EDGE,"E9.left"),sQuery(id+"F3.wireOp",EDGE,"E11.bottom"),sQuery(id+"F3.wireOp",EDGE,"E11.left"),sQuery(id+"F3.wireOp",EDGE,"E16.0"),sQuery(id+"F3.wireOp",EDGE,"E16.1")])]});
            var Q3;
            Q3=makeQuery(id+"F13.opExtrude","SWEPT_BODY",BODY,{"disambiguationData":[OSD([sQuery(id+"F12.wireOp",EDGE,"E30.bottom"),sQuery(id+"F12.wireOp",EDGE,"E30.right"),sQuery(id+"F12.wireOp",EDGE,"E31.0"),sQuery(id+"F12.wireOp",EDGE,"E33"),sQuery(id+"F12.wireOp",EDGE,"E34.0")])]});
            var Q4;
            Q4=makeQuery(id+"F26.opPattern","COPY",BODY,{"derivedFrom":makeQuery(id+"F10.opExtrude","SWEPT_BODY",BODY,{"disambiguationData":[OSD([sQuery(id+"F9.wireOp",EDGE,"E29.bottom"),sQuery(id+"F9.wireOp",EDGE,"E29.top"),sQuery(id+"F9.wireOp",EDGE,"E29.left"),sQuery(id+"F9.wireOp",EDGE,"E29.right")])]}),"instanceName":"1"});
            var Q5;
            Q5=makeQuery(id+"F27.opExtrude","SWEPT_BODY",BODY,{"disambiguationData":[OSD([sQuery(id+"F3.wireOp",EDGE,"E8.right"),sQuery(id+"F3.wireOp",EDGE,"E9.left"),sQuery(id+"F3.wireOp",EDGE,"E15"),sQuery(id+"F3.wireOp",EDGE,"E17"),sQuery(id+"F3.wireOp",EDGE,"E18.0"),sQuery(id+"F3.wireOp",EDGE,"E18.1")])]});
            var Q6;
            Q6=makeQuery(id+"F4.opExtrude","SWEPT_BODY",BODY,{"disambiguationData":[OSD([sQuery(id+"F3.wireOp",EDGE,"E9.bottom"),sQuery(id+"F3.wireOp",EDGE,"E9.right"),sQuery(id+"F3.wireOp",EDGE,"E10.right"),sQuery(id+"F3.wireOp",EDGE,"E17"),sQuery(id+"F3.wireOp",EDGE,"E20.0")])]});
            var Q7;
            Q7=makeQuery(id+"F15.opExtrude","SWEPT_BODY",BODY,{"disambiguationData":[OSD([sQuery(id+"F12.wireOp",EDGE,"E30.bottom"),sQuery(id+"F12.wireOp",EDGE,"E30.left"),sQuery(id+"F12.wireOp",EDGE,"E30.right"),sQuery(id+"F12.wireOp",EDGE,"E35.bottom")])]});
            var Q8;
            Q8=makeQuery(id+"F20.opExtrude","SWEPT_BODY",BODY,{"disambiguationData":[OSD([sQuery(id+"F3.wireOp",EDGE,"E8.bottom"),sQuery(id+"F3.wireOp",EDGE,"E12.1"),sQuery(id+"F3.wireOp",EDGE,"E13"),sQuery(id+"F3.wireOp",EDGE,"E14")])]});
            var Q9;
            Q9=makeQuery(id+"F21.opExtrude","SWEPT_BODY",BODY,{"disambiguationData":[OSD([sQuery(id+"F12.wireOp",EDGE,"E35.bottom"),sQuery(id+"F12.wireOp",EDGE,"E35.top"),sQuery(id+"F12.wireOp",EDGE,"E35.left"),sQuery(id+"F12.wireOp",EDGE,"E35.right")])]});
            var Q10;
            Q10=makeQuery(id+"F20.opExtrude","SWEPT_BODY",BODY,{"disambiguationData":[OSD([sQuery(id+"F3.wireOp",EDGE,"E9.bottom"),sQuery(id+"F3.wireOp",EDGE,"E20.0"),sQuery(id+"F3.wireOp",EDGE,"E21.0"),sQuery(id+"F3.wireOp",EDGE,"E23.0")])]});
            var Q11;
            Q11=makeQuery(id+"F4.opExtrude","SWEPT_BODY",BODY,{"disambiguationData":[OSD([sQuery(id+"F3.wireOp",EDGE,"E8.bottom"),sQuery(id+"F3.wireOp",EDGE,"E8.top"),sQuery(id+"F3.wireOp",EDGE,"E8.right"),sQuery(id+"F3.wireOp",EDGE,"E10.left"),sQuery(id+"F3.wireOp",EDGE,"E11.left"),sQuery(id+"F3.wireOp",EDGE,"E12.2"),sQuery(id+"F3.wireOp",EDGE,"E14")])]});
            var Q12;
            Q12=makeQuery(id+"F4.opExtrude","SWEPT_BODY",BODY,{"disambiguationData":[OSD([sQuery(id+"F3.wireOp",EDGE,"E9.bottom"),sQuery(id+"F3.wireOp",EDGE,"E9.left"),sQuery(id+"F3.wireOp",EDGE,"E17"),sQuery(id+"F3.wireOp",EDGE,"E21.0")])]});
            var Q13;
            Q13=makeQuery(id+"F26.opPattern","COPY",BODY,{"derivedFrom":makeQuery(id+"F15.opExtrude","SWEPT_BODY",BODY,{"disambiguationData":[OSD([sQuery(id+"F12.wireOp",EDGE,"E30.bottom"),sQuery(id+"F12.wireOp",EDGE,"E30.left"),sQuery(id+"F12.wireOp",EDGE,"E30.right"),sQuery(id+"F12.wireOp",EDGE,"E35.bottom")])]}),"instanceName":"1"});
            var Q14;
            Q14=makeQuery(id+"F4.opExtrude","SWEPT_BODY",BODY,{"disambiguationData":[OSD([sQuery(id+"F3.wireOp",EDGE,"E8.bottom"),sQuery(id+"F3.wireOp",EDGE,"E8.top"),sQuery(id+"F3.wireOp",EDGE,"E8.left"),sQuery(id+"F3.wireOp",EDGE,"E12.0"),sQuery(id+"F3.wireOp",EDGE,"E13")])]});
            var Q15;
            Q15=makeQuery(id+"F30.opExtrude","SWEPT_BODY",BODY,{"disambiguationData":[OSD([sQuery(id+"F29.wireOp",EDGE,"E42.bottom"),sQuery(id+"F29.wireOp",EDGE,"E42.top"),sQuery(id+"F29.wireOp",EDGE,"E42.left"),sQuery(id+"F29.wireOp",EDGE,"E42.right")])]});
            var Q16;
            Q16=makeQuery(id+"F30.opExtrude","SWEPT_BODY",BODY,{"disambiguationData":[OSD([sQuery(id+"F29.wireOp",EDGE,"E43.bottom"),sQuery(id+"F29.wireOp",EDGE,"E43.top"),sQuery(id+"F29.wireOp",EDGE,"E43.left"),sQuery(id+"F29.wireOp",EDGE,"E43.right")])]});
            var Q17;
            Q17=makeQuery(id+"F7.opExtrude","SWEPT_BODY",BODY,{"disambiguationData":[OSD([sQuery(id+"F5.wireOp",EDGE,"E24.right"),sQuery(id+"F5.wireOp",EDGE,"E26.top"),sQuery(id+"F5.wireOp",EDGE,"E26.left"),sQuery(id+"F5.wireOp",EDGE,"E26.right"),sQuery(id+"F5.wireOp",EDGE,"E28")])]});
            var Q18;
            Q18=makeQuery(id+"F7.opExtrude","SWEPT_BODY",BODY,{"disambiguationData":[OSD([sQuery(id+"F5.wireOp",EDGE,"E24.left"),sQuery(id+"F5.wireOp",EDGE,"E25.top"),sQuery(id+"F5.wireOp",EDGE,"E25.left"),sQuery(id+"F5.wireOp",EDGE,"E25.right"),sQuery(id+"F5.wireOp",EDGE,"E27")])]});
            var Q19;
            Q19=makeQuery(id+"F18.opExtrude","SWEPT_BODY",BODY,{"disambiguationData":[OSD([sQuery(id+"F17.wireOp",EDGE,"E39.bottom"),sQuery(id+"F17.wireOp",EDGE,"E39.top"),sQuery(id+"F17.wireOp",EDGE,"E39.left"),sQuery(id+"F17.wireOp",EDGE,"E39.right")])]});
            var Q20;
            Q20=makeQuery(id+"F14.opExtrude","SWEPT_BODY",BODY,{"disambiguationData":[OSD([sQuery(id+"F12.wireOp",EDGE,"E30.left"),sQuery(id+"F12.wireOp",EDGE,"E30.right"),sQuery(id+"F12.wireOp",EDGE,"E34.0"),sQuery(id+"F12.wireOp",EDGE,"E35.bottom")])]});
            var Q21;
            Q21=makeQuery(id+"F13.opExtrude","SWEPT_BODY",BODY,{"disambiguationData":[OSD([sQuery(id+"F12.wireOp",EDGE,"E30.bottom"),sQuery(id+"F12.wireOp",EDGE,"E30.left"),sQuery(id+"F12.wireOp",EDGE,"E31.2"),sQuery(id+"F12.wireOp",EDGE,"E32"),sQuery(id+"F12.wireOp",EDGE,"E34.0")])]});
            var Q22;
            Q22=makeQuery(id+"F6.opExtrude","SWEPT_BODY",BODY,{"disambiguationData":[OSD([sQuery(id+"F5.wireOp",EDGE,"E24.bottom"),sQuery(id+"F5.wireOp",EDGE,"E24.top"),sQuery(id+"F5.wireOp",EDGE,"E27"),sQuery(id+"F5.wireOp",EDGE,"E28")])]});
            var Q23;
            Q23=makeQuery(id+"F26.opPattern","COPY",BODY,{"derivedFrom":makeQuery(id+"F14.opExtrude","SWEPT_BODY",BODY,{"disambiguationData":[OSD([sQuery(id+"F12.wireOp",EDGE,"E30.left"),sQuery(id+"F12.wireOp",EDGE,"E30.right"),sQuery(id+"F12.wireOp",EDGE,"E34.0"),sQuery(id+"F12.wireOp",EDGE,"E35.bottom")])]}),"instanceName":"1"});
            var Q24;
            Q24=makeQuery(id+"F26.opPattern","COPY",BODY,{"derivedFrom":makeQuery(id+"F13.opExtrude","SWEPT_BODY",BODY,{"disambiguationData":[OSD([sQuery(id+"F12.wireOp",EDGE,"E30.bottom"),sQuery(id+"F12.wireOp",EDGE,"E30.right"),sQuery(id+"F12.wireOp",EDGE,"E31.0"),sQuery(id+"F12.wireOp",EDGE,"E33"),sQuery(id+"F12.wireOp",EDGE,"E34.0")])]}),"instanceName":"1"});
            var Q25;
            Q25=makeQuery(id+"F26.opPattern","COPY",BODY,{"derivedFrom":makeQuery(id+"F13.opExtrude","SWEPT_BODY",BODY,{"disambiguationData":[OSD([sQuery(id+"F12.wireOp",EDGE,"E30.bottom"),sQuery(id+"F12.wireOp",EDGE,"E30.left"),sQuery(id+"F12.wireOp",EDGE,"E31.2"),sQuery(id+"F12.wireOp",EDGE,"E32"),sQuery(id+"F12.wireOp",EDGE,"E34.0")])]}),"instanceName":"1"});
            var Q26;
            Q26=makeQuery(id+"F26.opPattern","COPY",BODY,{"derivedFrom":makeQuery(id+"F18.opExtrude","SWEPT_BODY",BODY,{"disambiguationData":[OSD([sQuery(id+"F17.wireOp",EDGE,"E39.bottom"),sQuery(id+"F17.wireOp",EDGE,"E39.top"),sQuery(id+"F17.wireOp",EDGE,"E39.left"),sQuery(id+"F17.wireOp",EDGE,"E39.right")])]}),"instanceName":"1"});
            var Q27;
            Q27=makeQuery(id+"F18.opExtrude","SWEPT_BODY",BODY,{"disambiguationData":[OSD([sQuery(id+"F17.wireOp",EDGE,"E36.bottom"),sQuery(id+"F17.wireOp",EDGE,"E36.top"),sQuery(id+"F17.wireOp",EDGE,"E36.left"),sQuery(id+"F17.wireOp",EDGE,"E36.right")])]});
            var Q28;
            Q28=makeQuery(id+"F26.opPattern","COPY",BODY,{"derivedFrom":makeQuery(id+"F18.opExtrude","SWEPT_BODY",BODY,{"disambiguationData":[OSD([sQuery(id+"F17.wireOp",EDGE,"E36.bottom"),sQuery(id+"F17.wireOp",EDGE,"E36.top"),sQuery(id+"F17.wireOp",EDGE,"E36.left"),sQuery(id+"F17.wireOp",EDGE,"E36.right")])]}),"instanceName":"1"});
            var Q29;
            Q29=makeQuery(id+"F31.opExtrude","SWEPT_BODY",BODY,{"disambiguationData":[OSD([sQuery(id+"F3.wireOp",EDGE,"E10.bottom"),sQuery(id+"F3.wireOp",EDGE,"E10.top"),sQuery(id+"F3.wireOp",EDGE,"E10.left"),sQuery(id+"F3.wireOp",EDGE,"E10.right")])]});
            var Q30;
            Q30=makeQuery(id+"F24.opExtrude","SWEPT_EDGE",EDGE,{"disambiguationData":[OSD([sQuery(id+"F1.wireOp",EDGE,"E7"),sQuery(id+"F23.wireOp",EDGE,"E41.bottom"),sQuery(id+"F23.wireOp",EDGE,"E41.left")])]});
            circularPattern(context, id + "F32", {"entities" : qUnion([Q0, Q1, Q2, Q3, Q4, Q5, Q6, Q7, Q8, Q9, Q10, Q11, Q12, Q13, Q14, Q15, Q16, Q17, Q18, Q19, Q20, Q21, Q22, Q23, Q24, Q25, Q26, Q27, Q28, Q29]), "axis" : qUnion([Q30]), "angle" : 180 * degree, "instanceCount" : 2, "equalSpace" : true});
        }
        {
            var Q0;
            Q0=makeQuery(id+"F32.opPattern","COPY",BODY,{"derivedFrom":makeQuery(id+"F14.opExtrude","SWEPT_BODY",BODY,{"disambiguationData":[OSD([sQuery(id+"F12.wireOp",EDGE,"E30.left"),sQuery(id+"F12.wireOp",EDGE,"E30.right"),sQuery(id+"F12.wireOp",EDGE,"E34.0"),sQuery(id+"F12.wireOp",EDGE,"E35.bottom")])]}),"instanceName":"1"});
            var Q1;
            Q1=makeQuery(id+"F32.opPattern","COPY",BODY,{"derivedFrom":makeQuery(id+"F15.opExtrude","SWEPT_BODY",BODY,{"disambiguationData":[OSD([sQuery(id+"F12.wireOp",EDGE,"E30.bottom"),sQuery(id+"F12.wireOp",EDGE,"E30.left"),sQuery(id+"F12.wireOp",EDGE,"E30.right"),sQuery(id+"F12.wireOp",EDGE,"E35.bottom")])]}),"instanceName":"1"});
            var Q2;
            Q2=makeQuery(id+"F32.opPattern","COPY",BODY,{"derivedFrom":makeQuery(id+"F13.opExtrude","SWEPT_BODY",BODY,{"disambiguationData":[OSD([sQuery(id+"F12.wireOp",EDGE,"E30.bottom"),sQuery(id+"F12.wireOp",EDGE,"E30.right"),sQuery(id+"F12.wireOp",EDGE,"E31.0"),sQuery(id+"F12.wireOp",EDGE,"E33"),sQuery(id+"F12.wireOp",EDGE,"E34.0")])]}),"instanceName":"1"});
            var Q3;
            Q3=makeQuery(id+"F32.opPattern","COPY",BODY,{"derivedFrom":makeQuery(id+"F13.opExtrude","SWEPT_BODY",BODY,{"disambiguationData":[OSD([sQuery(id+"F12.wireOp",EDGE,"E30.bottom"),sQuery(id+"F12.wireOp",EDGE,"E30.left"),sQuery(id+"F12.wireOp",EDGE,"E31.2"),sQuery(id+"F12.wireOp",EDGE,"E32"),sQuery(id+"F12.wireOp",EDGE,"E34.0")])]}),"instanceName":"1"});
            var Q4;
            Q4=makeQuery(id+"F32.opPattern","COPY",BODY,{"derivedFrom":makeQuery(id+"F10.opExtrude","SWEPT_BODY",BODY,{"disambiguationData":[OSD([sQuery(id+"F9.wireOp",EDGE,"E29.bottom"),sQuery(id+"F9.wireOp",EDGE,"E29.top"),sQuery(id+"F9.wireOp",EDGE,"E29.left"),sQuery(id+"F9.wireOp",EDGE,"E29.right")])]}),"instanceName":"1"});
            transform(context, id + "F33", {"entities" : qUnion([Q0, Q1, Q2, Q3, Q4]), "transformType" : TransformType.TRANSLATION_3D, "dx" : 0 * mm, "dy" : 415 * mm, "dz" : 0 * mm, "makeCopy" : true});
        }
        {
            var Q0;
            Q0=makeQuery(id+"F32.opPattern","COPY",FACE,{"derivedFrom":makeQuery(id+"F2.opExtrude","CAP_FACE",FACE,{"disambiguationData":[OSD([sQuery(id+"F1.wireOp",EDGE,"E6.bottom"),sQuery(id+"F1.wireOp",EDGE,"E6.left"),sQuery(id+"F1.wireOp",EDGE,"E6.right"),sQuery(id+"F1.wireOp",EDGE,"E7")])],"isStart":true}),"instanceName":"1"});
            extrude(context, id + "F34", {"entities" : qUnion([Q0]), "depth" : 2 * mm, "offsetDistance" : 25 * mm});
        }
        {
            var Q0;
            Q0=makeQuery(id+"F2.opExtrude","CAP_FACE",FACE,{"disambiguationData":[OSD([sQuery(id+"F1.wireOp",EDGE,"E6.bottom"),sQuery(id+"F1.wireOp",EDGE,"E6.left"),sQuery(id+"F1.wireOp",EDGE,"E6.right"),sQuery(id+"F1.wireOp",EDGE,"E7")])],"isStart":true});
            extrude(context, id + "F35", {"entities" : qUnion([Q0]), "depth" : 2 * mm, "offsetDistance" : 25 * mm});
        }
    });
